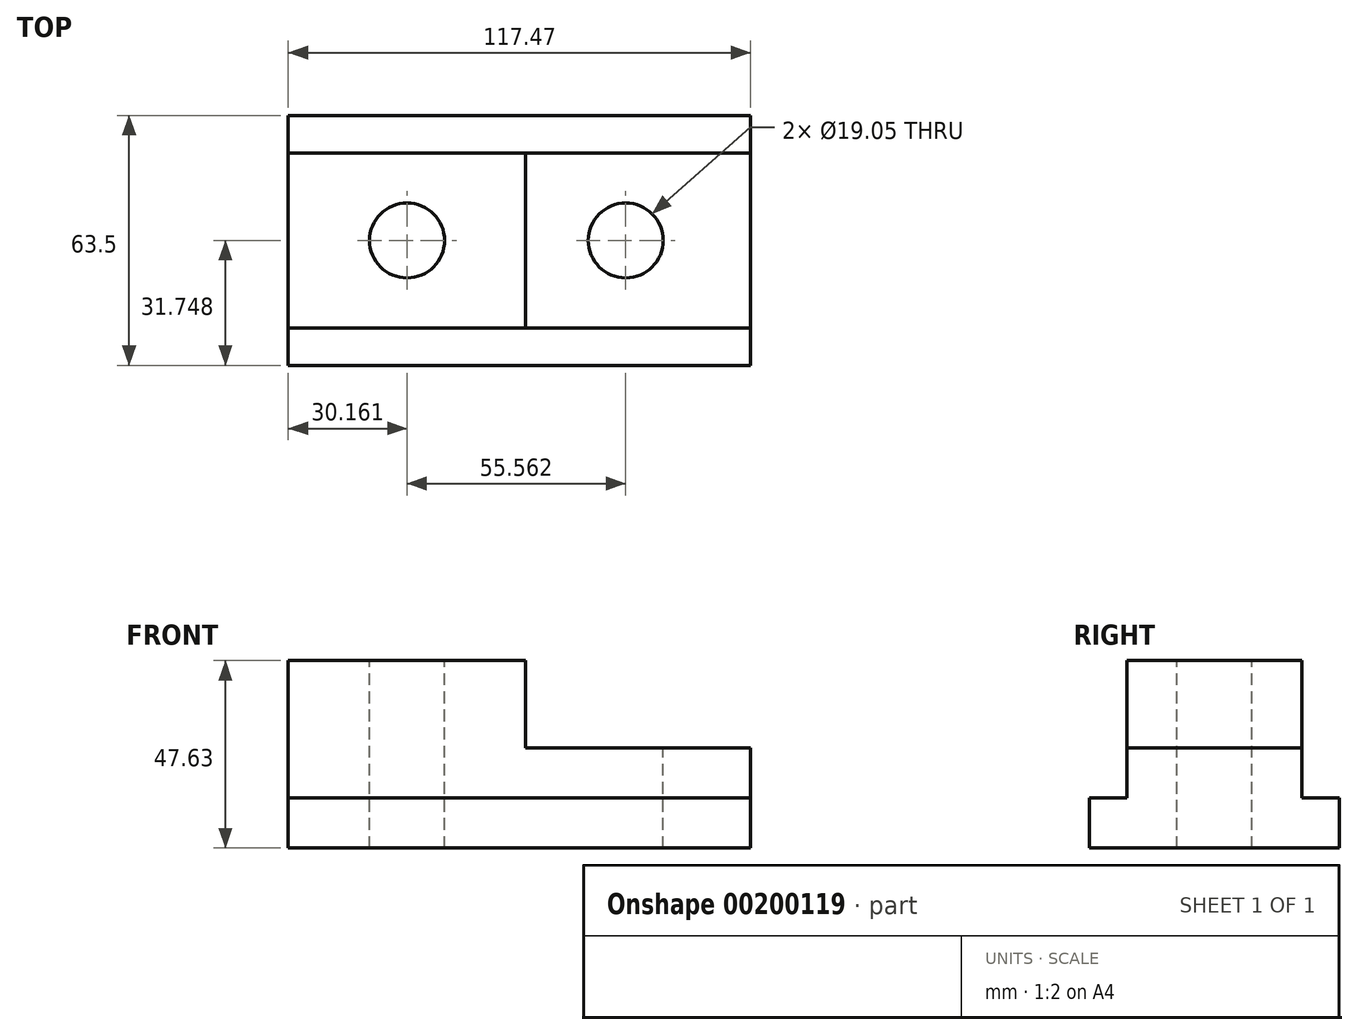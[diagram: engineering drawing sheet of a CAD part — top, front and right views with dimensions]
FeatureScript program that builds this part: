
annotation { "Feature Type Name" : "Feature", "Feature Type Description" : "" }
export const myFeature = defineFeature(function(context is Context, id is Id, definition is map)
    precondition{}
    {
        {
            var Q0;
            Q0=qCreatedBy(makeId("Top.planeOp"),FACE);
            var sketch = newSketch(context, id + "F0", { "sketchPlane" : qUnion([Q0])});
            skLineSegment(sketch, "E0.bottom", {"start": v(-47.8, -37.87) * mm, "end": v(69.68, -37.87) * mm});
            skLineSegment(sketch, "E0.top", {"start": v(-47.8, 25.63) * mm, "end": v(69.68, 25.63) * mm});
            skLineSegment(sketch, "E0.left", {"start": v(-47.8, -37.87) * mm, "end": v(-47.8, 25.63) * mm});
            skLineSegment(sketch, "E0.right", {"start": v(69.68, -37.87) * mm, "end": v(69.68, 25.63) * mm});
            skSolve(sketch);
        }
        {
            var Q0;
            Q0=makeQuery(id+"F0.imprint","IMPRINT",FACE,{"disambiguationData":[TD([[makeQuery(id+"F0.imprint","IMPRINT",EDGE,{"derivedFrom":sQuery(id+"F0.wireOp",EDGE,"E0.bottom")}),1.0]])]});
            extrude(context, id + "F1", {"entities" : qUnion([Q0]), "depth" : 12.7 * mm});
        }
        {
            var Q0;
            Q0=makeQuery(id+"F1.opExtrude","CAP_FACE",FACE,{"disambiguationData":[OSD([sQuery(id+"F0.wireOp",EDGE,"E0.bottom"),sQuery(id+"F0.wireOp",EDGE,"E0.top"),sQuery(id+"F0.wireOp",EDGE,"E0.left"),sQuery(id+"F0.wireOp",EDGE,"E0.right")])],"isStart":false});
            var sketch = newSketch(context, id + "F2", { "sketchPlane" : qUnion([Q0])});
            skLineSegment(sketch, "E1.bottom", {"start": v(-47.8, 16.1) * mm, "end": v(12.53, 16.1) * mm});
            skLineSegment(sketch, "E1.top", {"start": v(-47.8, -28.35) * mm, "end": v(12.53, -28.35) * mm});
            skLineSegment(sketch, "E1.left", {"start": v(-47.8, 16.1) * mm, "end": v(-47.8, -28.35) * mm});
            skLineSegment(sketch, "E1.right", {"start": v(12.53, 16.1) * mm, "end": v(12.53, -28.35) * mm});
            skLineSegment(sketch, "E2.bottom", {"start": v(12.53, 16.1) * mm, "end": v(69.68, 16.1) * mm});
            skLineSegment(sketch, "E2.top", {"start": v(12.53, -28.35) * mm, "end": v(69.68, -28.35) * mm});
            skLineSegment(sketch, "E2.right", {"start": v(69.68, 16.1) * mm, "end": v(69.68, -28.35) * mm});
            skSolve(sketch);
        }
        {
            var Q0;
            Q0=makeQuery(id+"F2.imprint","IMPRINT",FACE,{"disambiguationData":[TD([[makeQuery(id+"F2.imprint","IMPRINT",EDGE,{"derivedFrom":sQuery(id+"F2.wireOp",EDGE,"E1.bottom")}),-1.0]])]});
            extrude(context, id + "F3", {"entities" : qUnion([Q0]), "operationType" : NewBodyOperationType.ADD, "depth" : 34.92 * mm});
        }
        {
            var Q0;
            Q0=makeQuery(id+"F2.imprint","IMPRINT",FACE,{"disambiguationData":[TD([[makeQuery(id+"F2.imprint","IMPRINT",EDGE,{"derivedFrom":sQuery(id+"F2.wireOp",EDGE,"E2.bottom")}),-1.0]])]});
            extrude(context, id + "F4", {"entities" : qUnion([Q0]), "operationType" : NewBodyOperationType.ADD, "depth" : 12.7 * mm});
        }
        {
            var Q0;
            Q0=makeQuery(id+"F3.opExtrude","CAP_FACE",FACE,{"disambiguationData":[OSD([sQuery(id+"F2.wireOp",EDGE,"E1.bottom"),sQuery(id+"F2.wireOp",EDGE,"E1.top"),sQuery(id+"F2.wireOp",EDGE,"E1.left"),sQuery(id+"F2.wireOp",EDGE,"E1.right")])],"isStart":false});
            var sketch = newSketch(context, id + "F5", { "sketchPlane" : qUnion([Q0])});
            skCircle(sketch, "E3", {"center": v(-17.63, -6.12) * mm, "radius": 9.53 * mm});
            skSolve(sketch);
        }
        {
            var Q0;
            Q0=makeQuery(id+"F5.imprint","IMPRINT",FACE,{"disambiguationData":[TD([[makeQuery(id+"F5.imprint","IMPRINT",EDGE,{"derivedFrom":sQuery(id+"F5.wireOp",EDGE,"E3")}),1.0]])]});
            extrude(context, id + "F6", {"entities" : qUnion([Q0]), "operationType" : NewBodyOperationType.REMOVE, "oppositeDirection" : true, "depth" : 64.77 * mm});
        }
        {
            var Q0;
            Q0=makeQuery(id+"F4.opExtrude","CAP_FACE",FACE,{"disambiguationData":[OSD([sQuery(id+"F2.wireOp",EDGE,"E2.bottom"),sQuery(id+"F2.wireOp",EDGE,"E2.top"),sQuery(id+"F2.wireOp",EDGE,"E1.right"),sQuery(id+"F2.wireOp",EDGE,"E2.right")])],"isStart":false});
            var sketch = newSketch(context, id + "F7", { "sketchPlane" : qUnion([Q0])});
            skCircle(sketch, "E4", {"center": v(37.93, -6.12) * mm, "radius": 9.53 * mm});
            skSolve(sketch);
        }
        {
            var Q0;
            Q0=makeQuery(id+"F7.imprint","IMPRINT",FACE,{"disambiguationData":[TD([[makeQuery(id+"F7.imprint","IMPRINT",EDGE,{"derivedFrom":sQuery(id+"F7.wireOp",EDGE,"E4")}),1.0]])]});
            extrude(context, id + "F8", {"entities" : qUnion([Q0]), "operationType" : NewBodyOperationType.REMOVE, "oppositeDirection" : true, "depth" : 50.04 * mm});
        }
    });
